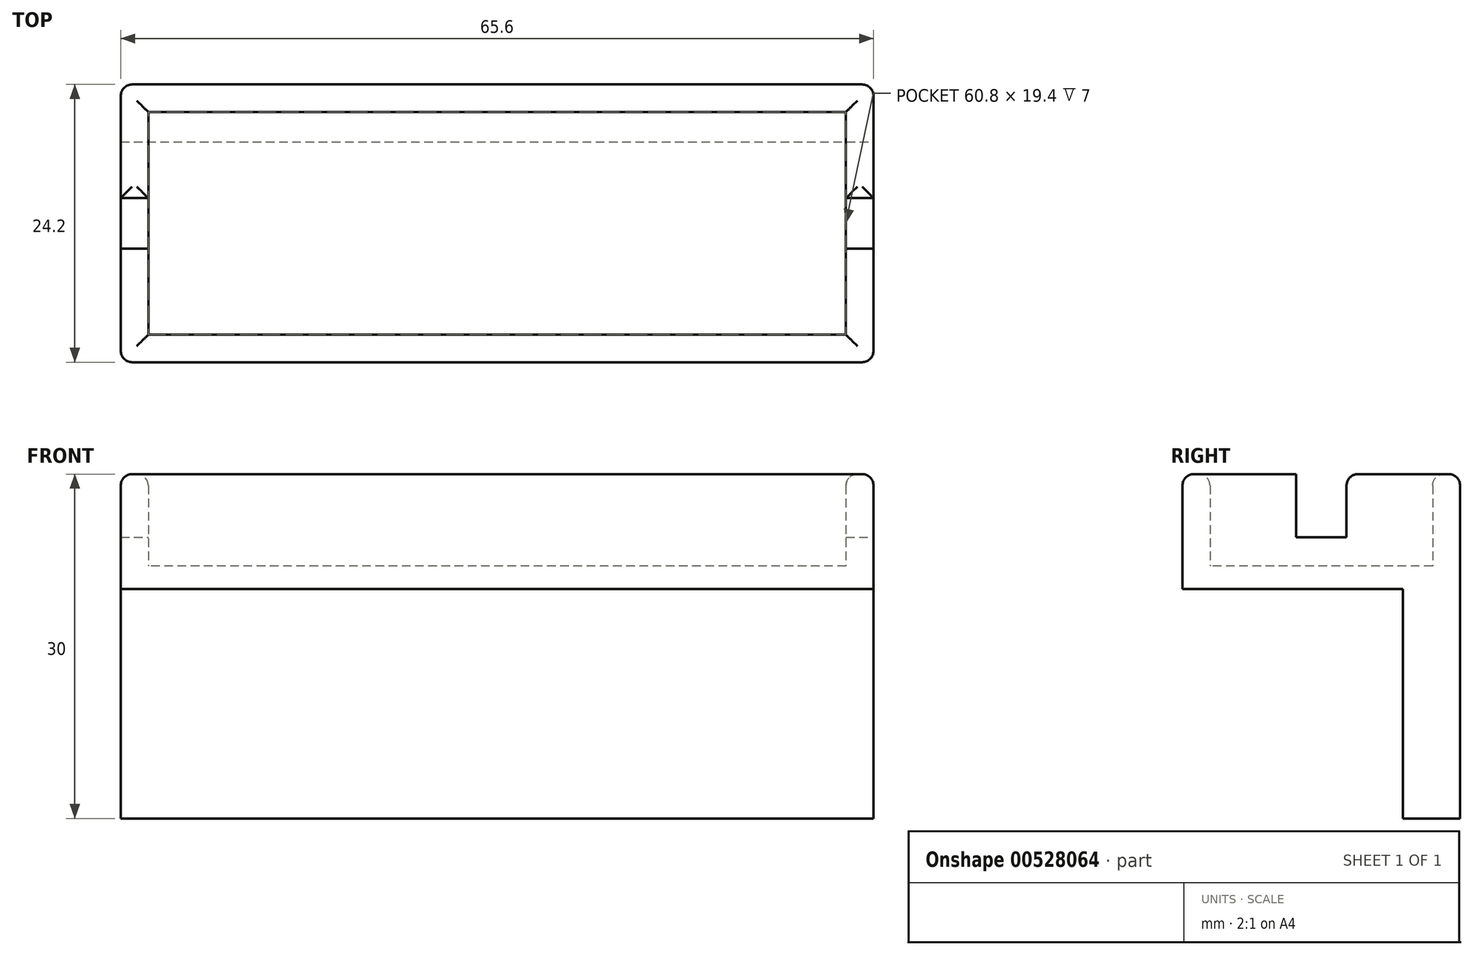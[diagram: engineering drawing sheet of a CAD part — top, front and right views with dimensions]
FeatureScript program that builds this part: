
annotation { "Feature Type Name" : "Feature", "Feature Type Description" : "" }
export const myFeature = defineFeature(function(context is Context, id is Id, definition is map)
    precondition{}
    {
        {
            var Q0;
            Q0=qCreatedBy(makeId("Top.planeOp"),FACE);
            var sketch = newSketch(context, id + "F0", { "sketchPlane" : qUnion([Q0])});
            skLineSegment(sketch, "E0.bottom", {"start": v(-32.8, 12.1) * mm, "end": v(32.8, 12.1) * mm});
            skLineSegment(sketch, "E0.top", {"start": v(-32.8, -12.1) * mm, "end": v(32.8, -12.1) * mm});
            skLineSegment(sketch, "E0.left", {"start": v(-32.8, 12.1) * mm, "end": v(-32.8, -12.1) * mm});
            skLineSegment(sketch, "E0.right", {"start": v(32.8, 12.1) * mm, "end": v(32.8, -12.1) * mm});
            skPoint(sketch, "E0.middle", {"position": v(0, 0) * mm});
            skLineSegment(sketch, "E1.bottom", {"start": v(30.4, 9.7) * mm, "end": v(-30.4, 9.7) * mm});
            skLineSegment(sketch, "E1.top", {"start": v(30.4, -9.7) * mm, "end": v(-30.4, -9.7) * mm});
            skLineSegment(sketch, "E1.left", {"start": v(30.4, 9.7) * mm, "end": v(30.4, -9.7) * mm});
            skLineSegment(sketch, "E1.right", {"start": v(-30.4, 9.7) * mm, "end": v(-30.4, -9.7) * mm});
            skSolve(sketch);
        }
        {
            var Q0;
            Q0 = qSketchRegion(id + "F0", true);
            extrude(context, id + "F1", {"entities" : qUnion([Q0]), "depth" : 10 * mm, "offsetDistance" : 25 * mm});
        }
        {
            var Q0;
            Q0=makeQuery(id+"F0.imprint","IMPRINT",FACE,{"disambiguationData":[TD([[makeQuery(id+"F0.imprint","IMPRINT",EDGE,{"derivedFrom":sQuery(id+"F0.wireOp",EDGE,"E1.bottom")}),1.0]])]});
            extrude(context, id + "F2", {"entities" : qUnion([Q0]), "operationType" : NewBodyOperationType.ADD, "depth" : 2 * mm, "offsetDistance" : 25 * mm});
        }
        {
            var Q0;
            Q0=makeQuery(id+"F1.opExtrude","SWEPT_FACE",FACE,{"disambiguationData":[OSD([sQuery(id+"F0.wireOp",EDGE,"E0.right")])]});
            var sketch = newSketch(context, id + "F3", { "sketchPlane" : qUnion([Q0])});
            skLineSegment(sketch, "E2.bottom", {"start": v(0, 10) * mm, "end": v(-2.2, 10) * mm});
            skLineSegment(sketch, "E2.top", {"start": v(0, 4.5) * mm, "end": v(-2.2, 4.5) * mm});
            skLineSegment(sketch, "E2.left", {"start": v(0, 10) * mm, "end": v(0, 4.5) * mm, "construction": true});
            skLineSegment(sketch, "E2.right", {"start": v(-2.2, 10) * mm, "end": v(-2.2, 4.5) * mm});
            skLineSegment(sketch, "E3.MirrorCS", {"start": v(0, 10) * mm, "end": v(2.2, 10) * mm});
            skLineSegment(sketch, "E4.MirrorCS", {"start": v(2.2, 10) * mm, "end": v(2.2, 4.5) * mm});
            skLineSegment(sketch, "E5.MirrorCS", {"start": v(0, 4.5) * mm, "end": v(2.2, 4.5) * mm});
            skSolve(sketch);
        }
        {
            var Q0;
            Q0 = qSketchRegion(id + "F3", true);
            extrude(context, id + "F4", {"entities" : qUnion([Q0]), "operationType" : NewBodyOperationType.REMOVE, "endBound" : BoundingType.THROUGH_ALL, "oppositeDirection" : true, "depth" : 25 * mm, "offsetDistance" : 25 * mm});
        }
        {
            var Q0;
            Q0=makeQuery(id+"F1.opExtrude","SWEPT_FACE",FACE,{"disambiguationData":[OSD([sQuery(id+"F0.wireOp",EDGE,"E0.bottom")])]});
            var sketch = newSketch(context, id + "F5", { "sketchPlane" : qUnion([Q0])});
            skLineSegment(sketch, "E6.bottom", {"start": v(-32.8, 0) * mm, "end": v(32.8, 0) * mm});
            skLineSegment(sketch, "E6.top", {"start": v(-32.8, -20) * mm, "end": v(32.8, -20) * mm});
            skLineSegment(sketch, "E6.left", {"start": v(-32.8, 0) * mm, "end": v(-32.8, -20) * mm});
            skLineSegment(sketch, "E6.right", {"start": v(32.8, 0) * mm, "end": v(32.8, -20) * mm});
            skSolve(sketch);
        }
        {
            var Q0;
            Q0 = qSketchRegion(id + "F5", true);
            extrude(context, id + "F6", {"entities" : qUnion([Q0]), "operationType" : NewBodyOperationType.ADD, "oppositeDirection" : true, "depth" : 5 * mm, "offsetDistance" : 25 * mm});
        }
        {
            var Q0;
            Q0=makeQuery(id+"F1.opExtrude","CAP_EDGE",EDGE,{"disambiguationData":[OSD([sQuery(id+"F0.wireOp",EDGE,"E1.top")])],"isStart":false});
            var Q1;
            Q1=makeQuery(id+"F1.opExtrude","CAP_EDGE",EDGE,{"disambiguationData":[OSD([sQuery(id+"F0.wireOp",EDGE,"E0.top")])],"isStart":false});
            var Q2;
            {var subQ0=sQuery(id+"F0.wireOp",EDGE,"E0.left");var subQ1=sQuery(id+"F0.wireOp",EDGE,"E0.top");Q2=makeQuery(id+"F4.boolean.opBoolean","SPLIT",EDGE,{"disambiguationData":[TD([makeQuery(id+"F1.opExtrude","SWEPT_FACE",FACE,{"disambiguationData":[OSD([subQ1])]})])],"derivedFrom":makeQuery(id+"F1.opExtrude","CAP_EDGE",EDGE,{"disambiguationData":[OSD([subQ0])],"isStart":false})});}
            var Q3;
            {var subQ0=sQuery(id+"F0.wireOp",EDGE,"E0.right");var subQ1=sQuery(id+"F0.wireOp",EDGE,"E0.top");Q3=makeQuery(id+"F4.boolean.opBoolean","SPLIT",EDGE,{"disambiguationData":[TD([makeQuery(id+"F1.opExtrude","SWEPT_FACE",FACE,{"disambiguationData":[OSD([subQ1])]})])],"derivedFrom":makeQuery(id+"F1.opExtrude","CAP_EDGE",EDGE,{"disambiguationData":[OSD([subQ0])],"isStart":false})});}
            var Q4;
            {var subQ0=sQuery(id+"F0.wireOp",EDGE,"E1.left");var subQ1=sQuery(id+"F0.wireOp",EDGE,"E1.top");Q4=makeQuery(id+"F4.boolean.opBoolean","SPLIT",EDGE,{"disambiguationData":[TD([makeQuery(id+"F1.opExtrude","SWEPT_FACE",FACE,{"disambiguationData":[OSD([subQ1])]})])],"derivedFrom":makeQuery(id+"F1.opExtrude","CAP_EDGE",EDGE,{"disambiguationData":[OSD([subQ0])],"isStart":false})});}
            var Q5;
            {var subQ1=sQuery(id+"F0.wireOp",EDGE,"E0.right");var subQ2=sQuery(id+"F0.wireOp",EDGE,"E0.left");var subQ3=sQuery(id+"F3.wireOp",EDGE,"E2.right");Q5=makeQuery(id+"F4.boolean.opBoolean","COPY",EDGE,{"disambiguationData":[TD([makeQuery(id+"F1.opExtrude","SWEPT_FACE",FACE,{"disambiguationData":[OSD([subQ2])]})])],"derivedFrom":makeQuery(id+"F4.opExtrude","SWEPT_EDGE",EDGE,{"disambiguationData":[OSD([subQ1,sQuery(id+"F3.wireOp",EDGE,"E2.bottom"),subQ3])]})});}
            var Q6;
            {var subQ1=sQuery(id+"F0.wireOp",EDGE,"E0.right");var subQ2=sQuery(id+"F3.wireOp",EDGE,"E2.right");Q6=makeQuery(id+"F4.boolean.opBoolean","COPY",EDGE,{"disambiguationData":[TD([makeQuery(id+"F1.opExtrude","SWEPT_FACE",FACE,{"disambiguationData":[OSD([subQ1])]})])],"derivedFrom":makeQuery(id+"F4.opExtrude","SWEPT_EDGE",EDGE,{"disambiguationData":[OSD([subQ1,sQuery(id+"F3.wireOp",EDGE,"E2.bottom"),subQ2])]})});}
            var Q7;
            {var subQ0=sQuery(id+"F0.wireOp",EDGE,"E1.right");var subQ1=sQuery(id+"F0.wireOp",EDGE,"E1.top");Q7=makeQuery(id+"F4.boolean.opBoolean","SPLIT",EDGE,{"disambiguationData":[TD([makeQuery(id+"F1.opExtrude","SWEPT_FACE",FACE,{"disambiguationData":[OSD([subQ1])]})])],"derivedFrom":makeQuery(id+"F1.opExtrude","CAP_EDGE",EDGE,{"disambiguationData":[OSD([subQ0])],"isStart":false})});}
            fillet(context, id + "F7", {"entities" : qUnion([Q0, Q1, Q2, Q3, Q4, Q5, Q6, Q7]), "radius" : 1 * mm, "tangentPropagation" : true, "allowEdgeOverflow" : false});
        }
        {
            var Q0;
            {var subQ1=sQuery(id+"F0.wireOp",EDGE,"E0.right");var subQ2=sQuery(id+"F0.wireOp",EDGE,"E0.left");var subQ3=sQuery(id+"F3.wireOp",EDGE,"E4.MirrorCS");Q0=makeQuery(id+"F4.boolean.opBoolean","COPY",EDGE,{"disambiguationData":[TD([makeQuery(id+"F1.opExtrude","SWEPT_FACE",FACE,{"disambiguationData":[OSD([subQ2])]})])],"derivedFrom":makeQuery(id+"F4.opExtrude","SWEPT_EDGE",EDGE,{"disambiguationData":[OSD([subQ1,sQuery(id+"F3.wireOp",EDGE,"E3.MirrorCS"),subQ3])]})});}
            var Q1;
            {var subQ1=sQuery(id+"F0.wireOp",EDGE,"E0.right");var subQ2=sQuery(id+"F3.wireOp",EDGE,"E4.MirrorCS");Q1=makeQuery(id+"F4.boolean.opBoolean","COPY",EDGE,{"disambiguationData":[TD([makeQuery(id+"F1.opExtrude","SWEPT_FACE",FACE,{"disambiguationData":[OSD([subQ1])]})])],"derivedFrom":makeQuery(id+"F4.opExtrude","SWEPT_EDGE",EDGE,{"disambiguationData":[OSD([subQ1,sQuery(id+"F3.wireOp",EDGE,"E3.MirrorCS"),subQ2])]})});}
            var Q2;
            {var subQ0=sQuery(id+"F0.wireOp",EDGE,"E0.bottom");var subQ1=sQuery(id+"F0.wireOp",EDGE,"E0.right");Q2=makeQuery(id+"F4.boolean.opBoolean","SPLIT",EDGE,{"disambiguationData":[TD([makeQuery(id+"F1.opExtrude","SWEPT_FACE",FACE,{"disambiguationData":[OSD([subQ0])]})])],"derivedFrom":makeQuery(id+"F1.opExtrude","CAP_EDGE",EDGE,{"disambiguationData":[OSD([subQ1])],"isStart":false})});}
            var Q3;
            {var subQ0=sQuery(id+"F0.wireOp",EDGE,"E0.bottom");var subQ1=sQuery(id+"F0.wireOp",EDGE,"E0.left");Q3=makeQuery(id+"F4.boolean.opBoolean","SPLIT",EDGE,{"disambiguationData":[TD([makeQuery(id+"F1.opExtrude","SWEPT_FACE",FACE,{"disambiguationData":[OSD([subQ0])]})])],"derivedFrom":makeQuery(id+"F1.opExtrude","CAP_EDGE",EDGE,{"disambiguationData":[OSD([subQ1])],"isStart":false})});}
            var Q4;
            {var subQ0=sQuery(id+"F0.wireOp",EDGE,"E1.right");var subQ1=sQuery(id+"F0.wireOp",EDGE,"E1.bottom");Q4=makeQuery(id+"F4.boolean.opBoolean","SPLIT",EDGE,{"disambiguationData":[TD([makeQuery(id+"F1.opExtrude","SWEPT_FACE",FACE,{"disambiguationData":[OSD([subQ1])]})])],"derivedFrom":makeQuery(id+"F1.opExtrude","CAP_EDGE",EDGE,{"disambiguationData":[OSD([subQ0])],"isStart":false})});}
            var Q5;
            {var subQ0=sQuery(id+"F0.wireOp",EDGE,"E1.left");var subQ1=sQuery(id+"F0.wireOp",EDGE,"E1.bottom");Q5=makeQuery(id+"F4.boolean.opBoolean","SPLIT",EDGE,{"disambiguationData":[TD([makeQuery(id+"F1.opExtrude","SWEPT_FACE",FACE,{"disambiguationData":[OSD([subQ1])]})])],"derivedFrom":makeQuery(id+"F1.opExtrude","CAP_EDGE",EDGE,{"disambiguationData":[OSD([subQ0])],"isStart":false})});}
            var Q6;
            Q6=makeQuery(id+"F1.opExtrude","CAP_EDGE",EDGE,{"disambiguationData":[OSD([sQuery(id+"F0.wireOp",EDGE,"E1.bottom")])],"isStart":false});
            var Q7;
            Q7=makeQuery(id+"F1.opExtrude","CAP_EDGE",EDGE,{"disambiguationData":[OSD([sQuery(id+"F0.wireOp",EDGE,"E0.bottom")])],"isStart":false});
            fillet(context, id + "F8", {"entities" : qUnion([Q0, Q1, Q2, Q3, Q4, Q5, Q6, Q7]), "radius" : 1 * mm, "tangentPropagation" : true, "allowEdgeOverflow" : false});
        }
        {
            var Q0;
            Q0=makeQuery(id+"F6.boolean.opBoolean","MERGE",EDGE,{"derivedFrom":[makeQuery(id+"F1.opExtrude","SWEPT_EDGE",EDGE,{"disambiguationData":[OSD([sQuery(id+"F0.wireOp",EDGE,"E0.bottom"),sQuery(id+"F0.wireOp",EDGE,"E0.right")])]}),makeQuery(id+"F6.opExtrude","CAP_EDGE",EDGE,{"disambiguationData":[OSD([sQuery(id+"F5.wireOp",EDGE,"E6.left")])],"isStart":true})]});
            var Q1;
            Q1=makeQuery(id+"F1.opExtrude","SWEPT_EDGE",EDGE,{"disambiguationData":[OSD([sQuery(id+"F0.wireOp",EDGE,"E0.top"),sQuery(id+"F0.wireOp",EDGE,"E0.right")])]});
            var Q2;
            Q2=makeQuery(id+"F6.boolean.opBoolean","MERGE",EDGE,{"derivedFrom":[makeQuery(id+"F1.opExtrude","SWEPT_EDGE",EDGE,{"disambiguationData":[OSD([sQuery(id+"F0.wireOp",EDGE,"E0.bottom"),sQuery(id+"F0.wireOp",EDGE,"E0.left")])]}),makeQuery(id+"F6.opExtrude","CAP_EDGE",EDGE,{"disambiguationData":[OSD([sQuery(id+"F5.wireOp",EDGE,"E6.right")])],"isStart":true})]});
            var Q3;
            Q3=makeQuery(id+"F1.opExtrude","SWEPT_EDGE",EDGE,{"disambiguationData":[OSD([sQuery(id+"F0.wireOp",EDGE,"E0.top"),sQuery(id+"F0.wireOp",EDGE,"E0.left")])]});
            fillet(context, id + "F9", {"entities" : qUnion([Q0, Q1, Q2, Q3]), "radius" : 1 * mm, "tangentPropagation" : true, "allowEdgeOverflow" : false});
        }
    });
